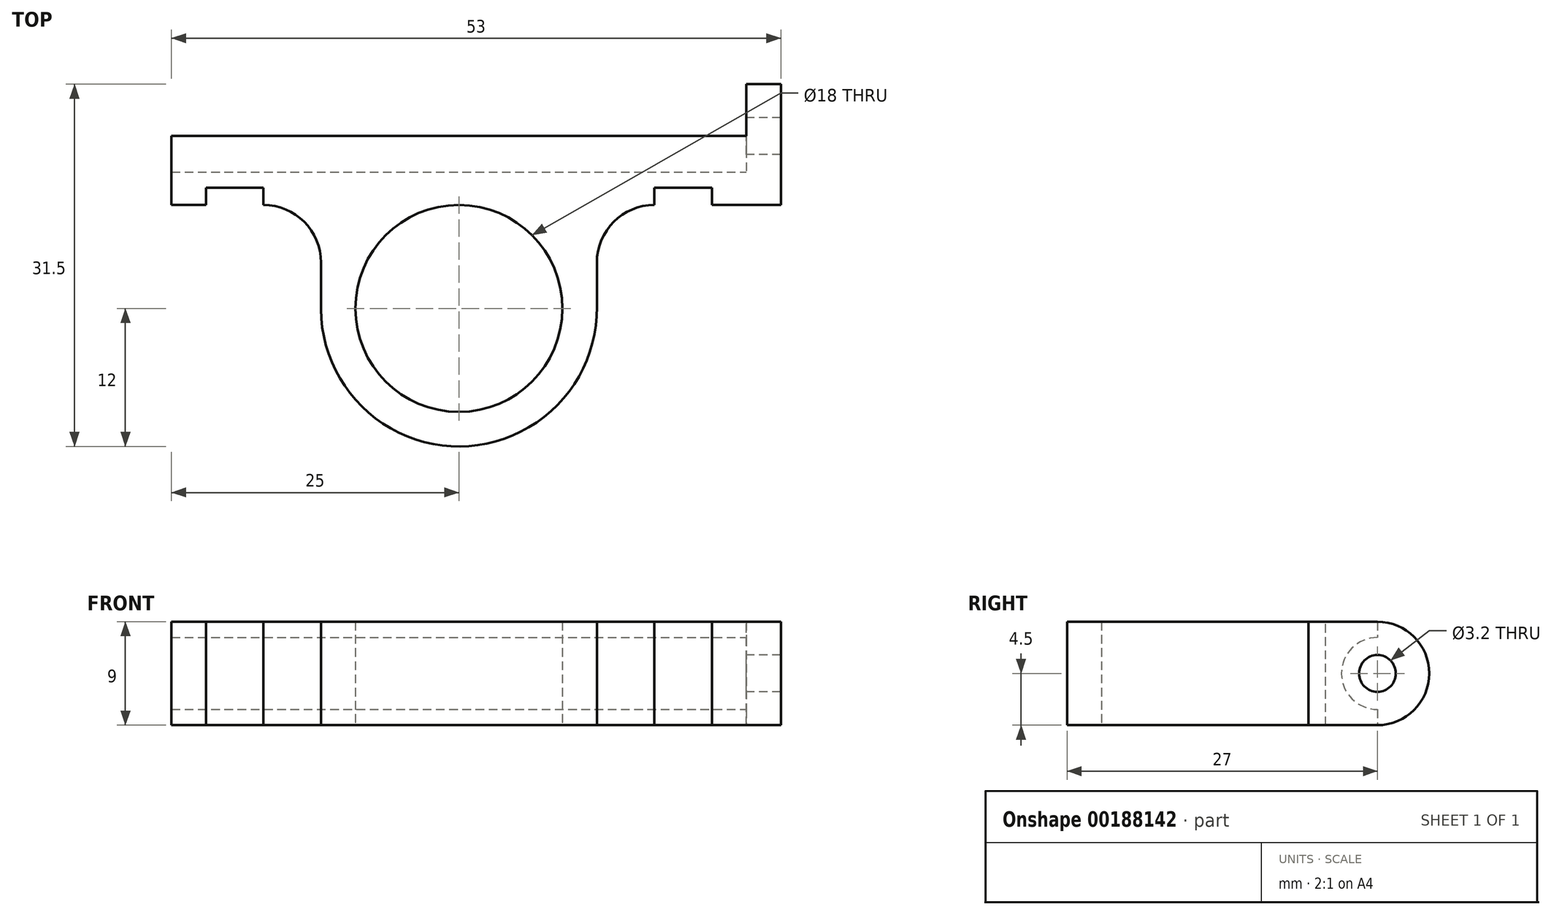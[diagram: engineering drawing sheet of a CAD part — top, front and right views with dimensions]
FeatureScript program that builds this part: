
annotation { "Feature Type Name" : "Feature", "Feature Type Description" : "" }
export const myFeature = defineFeature(function(context is Context, id is Id, definition is map)
    precondition{}
    {
        {
            var Q0;
            Q0=qCreatedBy(makeId("Top.planeOp"),FACE);
            var sketch = newSketch(context, id + "F0", { "sketchPlane" : qUnion([Q0])});
            skLineSegment(sketch, "E0", {"start": v(0, 0) * mm, "end": v(50, 0) * mm});
            skLineSegment(sketch, "E1", {"start": v(50, 0) * mm, "end": v(50, -6) * mm});
            skLineSegment(sketch, "E2", {"start": v(50, -6) * mm, "end": v(42, -6) * mm});
            skLineSegment(sketch, "E3", {"start": v(37, -6) * mm, "end": v(37, -6) * mm});
            skLineSegment(sketch, "E4", {"start": v(8, -6) * mm, "end": v(0, -6) * mm});
            skLineSegment(sketch, "E5", {"start": v(0, -6) * mm, "end": v(0, 0) * mm});
            skLineSegment(sketch, "E6", {"start": v(25, -6) * mm, "end": v(25, -15) * mm, "construction": true});
            skArc(sketch, "E7", {"start": v(13, -14.93) * mm, "mid": v(25.02, -27) * mm, "end": v(37, -14.9) * mm});
            skCircle(sketch, "E8", {"center": v(25, -15) * mm, "radius": 9 * mm});
            skLineSegment(sketch, "E9", {"start": v(37, -14.9) * mm, "end": v(37, -11) * mm});
            skLineSegment(sketch, "E10", {"start": v(13, -15.07) * mm, "end": v(13, -11) * mm});
            skPoint(sketch, "E11.visualSharp", {"position": v(13, -6) * mm});
            skArc(sketch, "E11.filletArc", {"start": v(13, -11) * mm, "mid": v(11.54, -7.46) * mm, "end": v(8, -6) * mm});
            skPoint(sketch, "E12.newPointA", {"position": v(37, -6) * mm});
            skArc(sketch, "E12.filletArc", {"start": v(42, -6) * mm, "mid": v(38.46, -7.46) * mm, "end": v(37, -11) * mm});
            skSolve(sketch);
        }
        {
            var Q0;
            Q0=makeQuery(id+"F0.imprint","IMPRINT",FACE,{"disambiguationData":[TD([[makeQuery(id+"F0.imprint","IMPRINT",EDGE,{"derivedFrom":sQuery(id+"F0.wireOp",EDGE,"E0")}),-1.0]])]});
            extrude(context, id + "F1", {"entities" : qUnion([Q0]), "depth" : 9 * mm});
        }
        {
            var Q0;
            Q0=makeQuery(id+"F1.opExtrude","SWEPT_FACE",FACE,{"disambiguationData":[OSD([sQuery(id+"F0.wireOp",EDGE,"E1")])]});
            var sketch = newSketch(context, id + "F2", { "sketchPlane" : qUnion([Q0])});
            skLineSegment(sketch, "E13", {"start": v(0, 9) * mm, "end": v(0, 4.5) * mm, "construction": true});
            skCircle(sketch, "E14", {"center": v(0, 4.5) * mm, "radius": 3.12 * mm});
            skSolve(sketch);
        }
        {
            var Q0;
            {var subQ0=sQuery(id+"F2.wireOp",EDGE,"E14");var subQ1=makeQuery(id+"F1.opExtrude","SWEPT_EDGE",EDGE,{"disambiguationData":[OSD([sQuery(id+"F0.wireOp",EDGE,"E0"),sQuery(id+"F0.wireOp",EDGE,"E1")])]});var subQ2=makeQuery(id+"F2.imprint","INTERSECT",VERTEX,{"disambiguationData":[OD(0.0)],"derivedFrom":[subQ1,subQ0]});Q0=makeQuery(id+"F2.imprint","IMPRINT",FACE,{"disambiguationData":[TD([[makeQuery(id+"F2.imprint","IMPRINT",EDGE,{"disambiguationData":[TD([[subQ2,1.0]])],"derivedFrom":subQ0}),1.0]])]});}
            extrude(context, id + "F3", {"entities" : qUnion([Q0]), "operationType" : NewBodyOperationType.REMOVE, "oppositeDirection" : true, "depth" : 50 * mm});
        }
        {
            var Q0;
            Q0=makeQuery(id+"F1.opExtrude","SWEPT_FACE",FACE,{"disambiguationData":[OSD([sQuery(id+"F0.wireOp",EDGE,"E1")])]});
            var sketch = newSketch(context, id + "F4", { "sketchPlane" : qUnion([Q0])});
            skCircle(sketch, "E15", {"center": v(0, 4.5) * mm, "radius": 1.6 * mm});
            skArc(sketch, "E16", {"start": v(0, 0) * mm, "mid": v(4.5, 4.5) * mm, "end": v(0, 9) * mm});
            skLineSegment(sketch, "E17.bottom", {"start": v(0, 9) * mm, "end": v(-6, 9) * mm});
            skLineSegment(sketch, "E17.top", {"start": v(0, 0) * mm, "end": v(-6, 0) * mm});
            skLineSegment(sketch, "E17.left", {"start": v(0, 6.1) * mm, "end": v(0, 2.9) * mm});
            skLineSegment(sketch, "E17.right", {"start": v(-6, 9) * mm, "end": v(-6, 0) * mm});
            skSolve(sketch);
        }
        {
            var Q0;
            Q0=makeQuery(id+"F4.imprint","IMPRINT",FACE,{"disambiguationData":[TD([[makeQuery(id+"F4.imprint","IMPRINT",EDGE,{"derivedFrom":sQuery(id+"F4.wireOp",EDGE,"E16")}),1.0]])]});
            var Q1;
            Q1=makeQuery(id+"F4.imprint","IMPRINT",FACE,{"disambiguationData":[TD([[makeQuery(id+"F4.imprint","IMPRINT",EDGE,{"derivedFrom":sQuery(id+"F4.wireOp",EDGE,"E17.bottom")}),1.0]])]});
            extrude(context, id + "F5", {"entities" : qUnion([Q0, Q1]), "operationType" : NewBodyOperationType.ADD, "depth" : 3 * mm});
        }
        {
            var Q0;
            Q0=makeQuery(id+"F5.boolean.opBoolean","MERGE",FACE,{"derivedFrom":[makeQuery(id+"F1.opExtrude","CAP_FACE",FACE,{"disambiguationData":[OSD([sQuery(id+"F0.wireOp",EDGE,"E0"),sQuery(id+"F0.wireOp",EDGE,"E1"),sQuery(id+"F0.wireOp",EDGE,"E2"),sQuery(id+"F0.wireOp",EDGE,"E4"),sQuery(id+"F0.wireOp",EDGE,"E5"),sQuery(id+"F0.wireOp",EDGE,"E7"),sQuery(id+"F0.wireOp",EDGE,"E8"),sQuery(id+"F0.wireOp",EDGE,"E9"),sQuery(id+"F0.wireOp",EDGE,"E10"),sQuery(id+"F0.wireOp",EDGE,"E11.filletArc"),sQuery(id+"F0.wireOp",EDGE,"E12.filletArc")])],"isStart":false}),makeQuery(id+"F5.opExtrude","SWEPT_FACE",FACE,{"disambiguationData":[OSD([sQuery(id+"F4.wireOp",EDGE,"E17.bottom")])]})]});
            var sketch = newSketch(context, id + "F6", { "sketchPlane" : qUnion([Q0])});
            skLineSegment(sketch, "E18", {"start": v(53, -6) * mm, "end": v(47, -6) * mm, "construction": true});
            skLineSegment(sketch, "E19", {"start": v(0, -6) * mm, "end": v(3, -6) * mm, "construction": true});
            skLineSegment(sketch, "E20.bottom", {"start": v(3, -6) * mm, "end": v(8, -6) * mm});
            skLineSegment(sketch, "E20.top", {"start": v(3, -4.5) * mm, "end": v(8, -4.5) * mm});
            skLineSegment(sketch, "E20.left", {"start": v(3, -6) * mm, "end": v(3, -4.5) * mm});
            skLineSegment(sketch, "E20.right", {"start": v(8, -6) * mm, "end": v(8, -4.5) * mm});
            skLineSegment(sketch, "E21.bottom", {"start": v(47, -6) * mm, "end": v(42, -6) * mm});
            skLineSegment(sketch, "E21.top", {"start": v(47, -4.5) * mm, "end": v(42, -4.5) * mm});
            skLineSegment(sketch, "E21.left", {"start": v(47, -6) * mm, "end": v(47, -4.5) * mm});
            skLineSegment(sketch, "E21.right", {"start": v(42, -6) * mm, "end": v(42, -4.5) * mm});
            skSolve(sketch);
        }
        {
            var Q0;
            Q0 = qSketchRegion(id + "F6", true);
            extrude(context, id + "F7", {"entities" : qUnion([Q0]), "operationType" : NewBodyOperationType.REMOVE, "oppositeDirection" : true, "depth" : 25 * mm});
        }
    });
